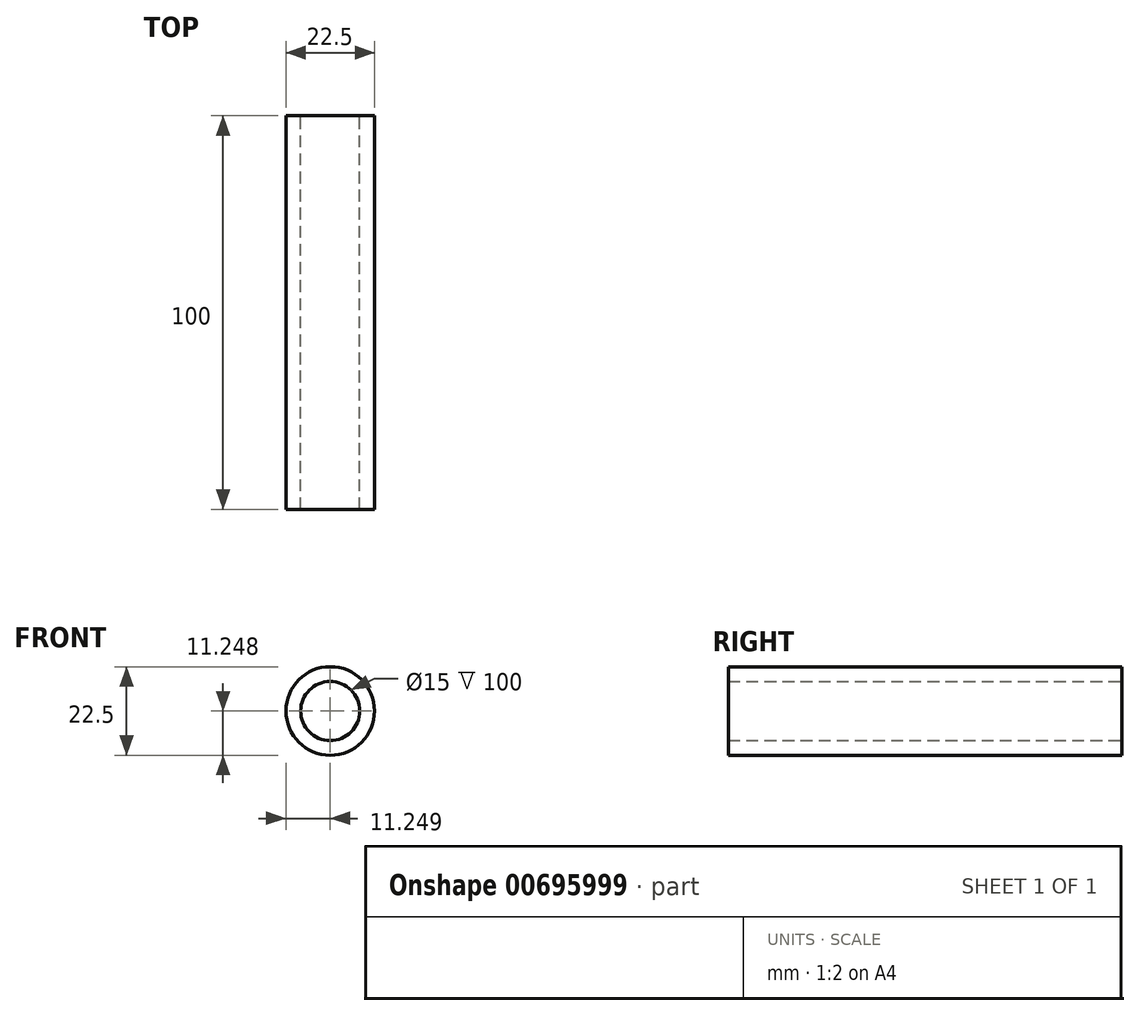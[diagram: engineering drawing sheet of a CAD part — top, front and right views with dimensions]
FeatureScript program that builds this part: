
annotation { "Feature Type Name" : "Feature", "Feature Type Description" : "" }
export const myFeature = defineFeature(function(context is Context, id is Id, definition is map)
    precondition{}
    {
        {
            var Q0;
            Q0=qCreatedBy(makeId("Front.planeOp"),FACE);
            var sketch = newSketch(context, id + "F0", { "sketchPlane" : qUnion([Q0])});
            skCircle(sketch, "E0", {"center": v(-14.82, 18.92) * mm, "radius": 7.5 * mm});
            skCircle(sketch, "E1", {"center": v(-14.82, 18.92) * mm, "radius": 11.25 * mm});
            skSolve(sketch);
        }
        {
            var Q0;
            Q0=makeQuery(id+"F0.imprint","IMPRINT",FACE,{"disambiguationData":[TD([[makeQuery(id+"F0.imprint","IMPRINT",EDGE,{"derivedFrom":sQuery(id+"F0.wireOp",EDGE,"E0")}),-1.0]])]});
            extrude(context, id + "F1", {"entities" : qUnion([Q0]), "depth" : 100 * mm, "offsetDistance" : 25 * mm});
        }
    });
